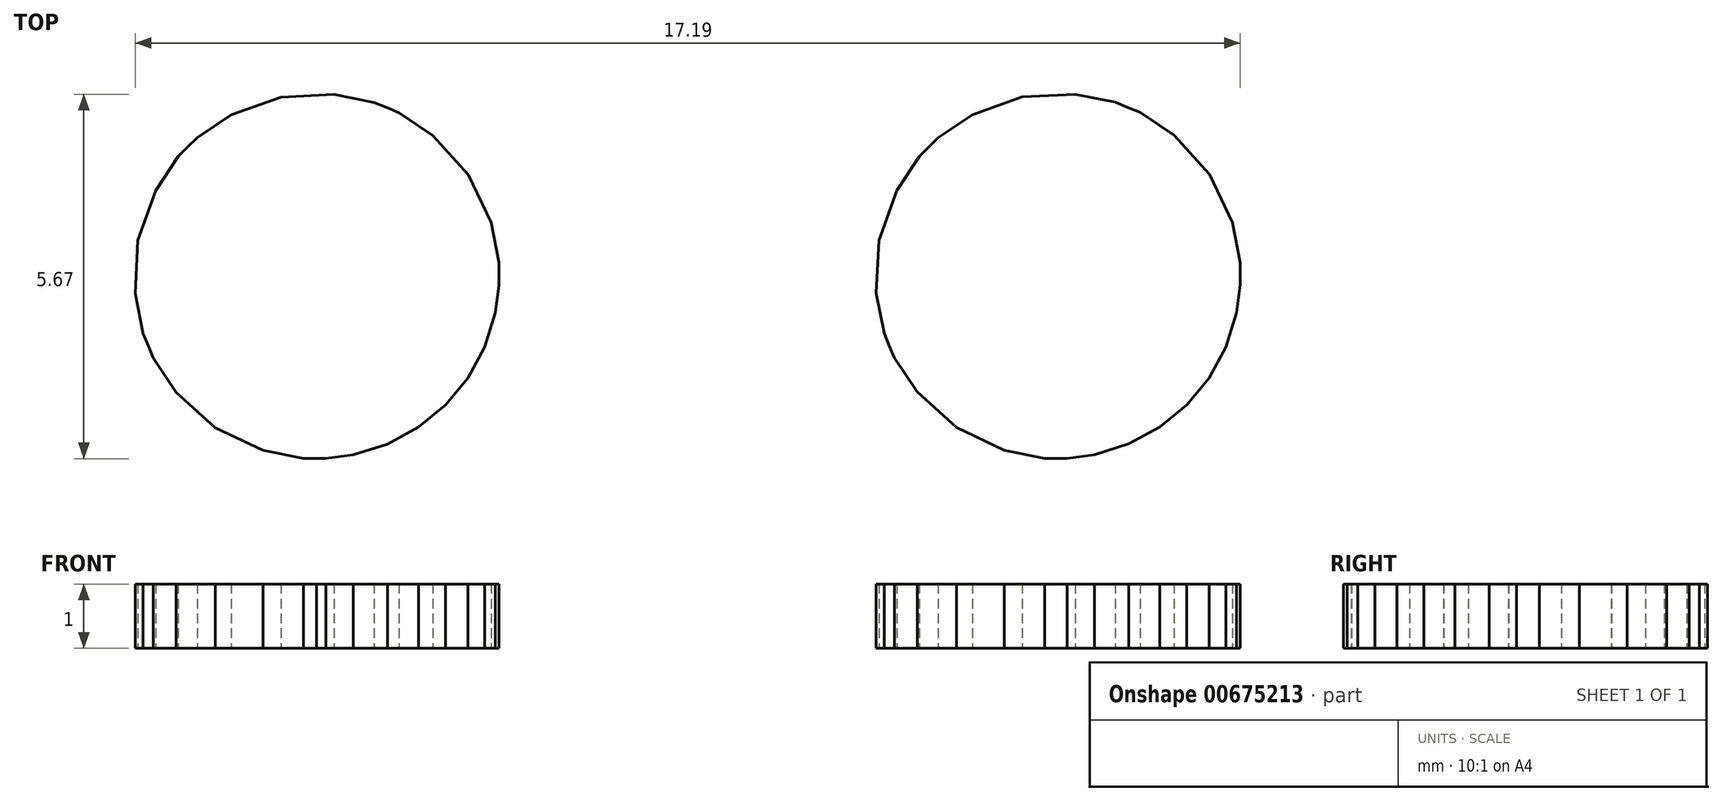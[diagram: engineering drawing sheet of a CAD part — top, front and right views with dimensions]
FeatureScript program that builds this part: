
annotation { "Feature Type Name" : "Feature", "Feature Type Description" : "" }
export const myFeature = defineFeature(function(context is Context, id is Id, definition is map)
    precondition{}
    {
        {
            var Q0;
            Q0=qCreatedBy(makeId("Top.planeOp"),FACE);
            var sketch = newSketch(context, id + "F0", { "sketchPlane" : qUnion([Q0])});
            skLineSegment(sketch, "E0", {"start": v(20.61, 4.27) * mm, "end": v(20.61, 4.15) * mm});
            skLineSegment(sketch, "E1", {"start": v(20.61, 4.15) * mm, "end": v(20.52, 3.81) * mm});
            skLineSegment(sketch, "E2", {"start": v(20.52, 3.81) * mm, "end": v(20.27, 3.44) * mm});
            skLineSegment(sketch, "E3", {"start": v(20.27, 3.44) * mm, "end": v(19.9, 3.2) * mm});
            skLineSegment(sketch, "E4", {"start": v(19.9, 3.2) * mm, "end": v(19.56, 3.1) * mm});
            skLineSegment(sketch, "E5", {"start": v(19.56, 3.1) * mm, "end": v(19.45, 3.1) * mm});
            skLineSegment(sketch, "E6", {"start": v(19.45, 3.1) * mm, "end": v(19.34, 3.1) * mm});
            skLineSegment(sketch, "E7", {"start": v(19.34, 3.1) * mm, "end": v(19, 3.2) * mm});
            skLineSegment(sketch, "E8", {"start": v(19, 3.2) * mm, "end": v(18.63, 3.44) * mm});
            skLineSegment(sketch, "E9", {"start": v(18.63, 3.44) * mm, "end": v(18.38, 3.81) * mm});
            skLineSegment(sketch, "E10", {"start": v(18.38, 3.81) * mm, "end": v(18.29, 4.15) * mm});
            skLineSegment(sketch, "E11", {"start": v(18.29, 4.15) * mm, "end": v(18.29, 4.27) * mm});
            skLineSegment(sketch, "E12", {"start": v(18.29, 4.27) * mm, "end": v(18.29, 4.38) * mm});
            skLineSegment(sketch, "E13", {"start": v(18.29, 4.38) * mm, "end": v(18.38, 4.72) * mm});
            skLineSegment(sketch, "E14", {"start": v(18.38, 4.72) * mm, "end": v(18.63, 5.09) * mm});
            skLineSegment(sketch, "E15", {"start": v(18.63, 5.09) * mm, "end": v(19, 5.34) * mm});
            skLineSegment(sketch, "E16", {"start": v(19, 5.34) * mm, "end": v(19.34, 5.43) * mm});
            skLineSegment(sketch, "E17", {"start": v(19.34, 5.43) * mm, "end": v(19.45, 5.43) * mm});
            skLineSegment(sketch, "E18", {"start": v(19.45, 5.43) * mm, "end": v(19.56, 5.43) * mm});
            skLineSegment(sketch, "E19", {"start": v(19.56, 5.43) * mm, "end": v(19.9, 5.34) * mm});
            skLineSegment(sketch, "E20", {"start": v(19.9, 5.34) * mm, "end": v(20.27, 5.09) * mm});
            skLineSegment(sketch, "E21", {"start": v(20.27, 5.09) * mm, "end": v(20.52, 4.72) * mm});
            skLineSegment(sketch, "E22", {"start": v(20.52, 4.72) * mm, "end": v(20.61, 4.38) * mm});
            skLineSegment(sketch, "E23", {"start": v(20.61, 4.38) * mm, "end": v(20.61, 4.27) * mm});
            skLineSegment(sketch, "E24", {"start": v(14.75, 8) * mm, "end": v(12.79, 8) * mm});
            skLineSegment(sketch, "E25", {"start": v(12.79, 8) * mm, "end": v(12.79, 1.6) * mm});
            skLineSegment(sketch, "E26", {"start": v(12.79, 1.6) * mm, "end": v(11.27, 1.6) * mm});
            skLineSegment(sketch, "E27", {"start": v(11.27, 1.6) * mm, "end": v(11.27, -0.27) * mm});
            skLineSegment(sketch, "E28", {"start": v(11.27, -0.27) * mm, "end": v(12.79, -0.27) * mm});
            skLineSegment(sketch, "E29", {"start": v(12.79, -0.27) * mm, "end": v(12.79, -8) * mm});
            skLineSegment(sketch, "E30", {"start": v(12.79, -8) * mm, "end": v(14.75, -8) * mm});
            skLineSegment(sketch, "E31", {"start": v(14.75, -8) * mm, "end": v(14.75, -0.27) * mm});
            skLineSegment(sketch, "E32", {"start": v(14.75, -0.27) * mm, "end": v(16.9, -0.27) * mm});
            skLineSegment(sketch, "E33", {"start": v(16.9, -0.27) * mm, "end": v(16.9, 1.56) * mm});
            skLineSegment(sketch, "E34", {"start": v(16.9, 1.56) * mm, "end": v(14.75, 1.56) * mm});
            skLineSegment(sketch, "E35", {"start": v(14.75, 1.56) * mm, "end": v(14.75, 8) * mm});
            skLineSegment(sketch, "E36", {"start": v(5.3, 1.59) * mm, "end": v(5.12, 1.59) * mm});
            skLineSegment(sketch, "E37", {"start": v(5.12, 1.59) * mm, "end": v(4.59, 1.53) * mm});
            skLineSegment(sketch, "E38", {"start": v(4.59, 1.53) * mm, "end": v(3.9, 1.38) * mm});
            skLineSegment(sketch, "E39", {"start": v(3.9, 1.38) * mm, "end": v(3.25, 1.12) * mm});
            skLineSegment(sketch, "E40", {"start": v(3.25, 1.12) * mm, "end": v(2.65, 0.78) * mm});
            skLineSegment(sketch, "E41", {"start": v(2.65, 0.78) * mm, "end": v(2.1, 0.35) * mm});
            skLineSegment(sketch, "E42", {"start": v(2.1, 0.35) * mm, "end": v(1.62, -0.15) * mm});
            skLineSegment(sketch, "E43", {"start": v(1.62, -0.15) * mm, "end": v(1.2, -0.72) * mm});
            skLineSegment(sketch, "E44", {"start": v(1.2, -0.72) * mm, "end": v(0.95, -1.2) * mm});
            skLineSegment(sketch, "E45", {"start": v(0.95, -1.2) * mm, "end": v(0.88, -1.37) * mm});
            skLineSegment(sketch, "E46", {"start": v(0.88, -1.37) * mm, "end": v(0.82, -1.53) * mm});
            skLineSegment(sketch, "E47", {"start": v(0.82, -1.53) * mm, "end": v(0.66, -2.05) * mm});
            skLineSegment(sketch, "E48", {"start": v(0.66, -2.05) * mm, "end": v(0.54, -2.74) * mm});
            skLineSegment(sketch, "E49", {"start": v(0.54, -2.74) * mm, "end": v(0.53, -3.44) * mm});
            skLineSegment(sketch, "E50", {"start": v(0.53, -3.44) * mm, "end": v(0.61, -4.13) * mm});
            skLineSegment(sketch, "E51", {"start": v(0.61, -4.13) * mm, "end": v(0.8, -4.8) * mm});
            skLineSegment(sketch, "E52", {"start": v(0.8, -4.8) * mm, "end": v(1.08, -5.44) * mm});
            skLineSegment(sketch, "E53", {"start": v(1.08, -5.44) * mm, "end": v(1.45, -6.03) * mm});
            skLineSegment(sketch, "E54", {"start": v(1.45, -6.03) * mm, "end": v(1.8, -6.45) * mm});
            skLineSegment(sketch, "E55", {"start": v(1.8, -6.45) * mm, "end": v(1.92, -6.58) * mm});
            skLineSegment(sketch, "E56", {"start": v(1.92, -6.58) * mm, "end": v(2.05, -6.7) * mm});
            skLineSegment(sketch, "E57", {"start": v(2.05, -6.7) * mm, "end": v(2.46, -7.04) * mm});
            skLineSegment(sketch, "E58", {"start": v(2.46, -7.04) * mm, "end": v(3.06, -7.42) * mm});
            skLineSegment(sketch, "E59", {"start": v(3.06, -7.42) * mm, "end": v(3.7, -7.7) * mm});
            skLineSegment(sketch, "E60", {"start": v(3.7, -7.7) * mm, "end": v(4.37, -7.89) * mm});
            skLineSegment(sketch, "E61", {"start": v(4.37, -7.89) * mm, "end": v(5.06, -7.97) * mm});
            skLineSegment(sketch, "E62", {"start": v(5.06, -7.97) * mm, "end": v(5.76, -7.96) * mm});
            skLineSegment(sketch, "E63", {"start": v(5.76, -7.96) * mm, "end": v(6.45, -7.84) * mm});
            skLineSegment(sketch, "E64", {"start": v(6.45, -7.84) * mm, "end": v(6.97, -7.68) * mm});
            skLineSegment(sketch, "E65", {"start": v(6.97, -7.68) * mm, "end": v(7.13, -7.61) * mm});
            skLineSegment(sketch, "E66", {"start": v(7.13, -7.61) * mm, "end": v(7.3, -7.55) * mm});
            skLineSegment(sketch, "E67", {"start": v(7.3, -7.55) * mm, "end": v(7.77, -7.3) * mm});
            skLineSegment(sketch, "E68", {"start": v(7.77, -7.3) * mm, "end": v(8.35, -6.88) * mm});
            skLineSegment(sketch, "E69", {"start": v(8.35, -6.88) * mm, "end": v(8.85, -6.4) * mm});
            skLineSegment(sketch, "E70", {"start": v(8.85, -6.4) * mm, "end": v(9.28, -5.85) * mm});
            skLineSegment(sketch, "E71", {"start": v(9.28, -5.85) * mm, "end": v(9.62, -5.25) * mm});
            skLineSegment(sketch, "E72", {"start": v(9.62, -5.25) * mm, "end": v(9.87, -4.6) * mm});
            skLineSegment(sketch, "E73", {"start": v(9.87, -4.6) * mm, "end": v(10.03, -3.91) * mm});
            skLineSegment(sketch, "E74", {"start": v(10.03, -3.91) * mm, "end": v(10.08, -3.37) * mm});
            skLineSegment(sketch, "E75", {"start": v(10.08, -3.37) * mm, "end": v(10.08, -3.2) * mm});
            skLineSegment(sketch, "E76", {"start": v(10.08, -3.2) * mm, "end": v(10.08, -2.95) * mm});
            skLineSegment(sketch, "E77", {"start": v(10.08, -2.95) * mm, "end": v(9.99, -2.23) * mm});
            skLineSegment(sketch, "E78", {"start": v(9.99, -2.23) * mm, "end": v(9.7, -1.33) * mm});
            skLineSegment(sketch, "E79", {"start": v(9.7, -1.33) * mm, "end": v(9.27, -0.52) * mm});
            skLineSegment(sketch, "E80", {"start": v(9.27, -0.52) * mm, "end": v(8.68, 0.19) * mm});
            skLineSegment(sketch, "E81", {"start": v(8.68, 0.19) * mm, "end": v(7.98, 0.77) * mm});
            skLineSegment(sketch, "E82", {"start": v(7.98, 0.77) * mm, "end": v(7.16, 1.21) * mm});
            skLineSegment(sketch, "E83", {"start": v(7.16, 1.21) * mm, "end": v(6.27, 1.49) * mm});
            skLineSegment(sketch, "E84", {"start": v(6.27, 1.49) * mm, "end": v(5.54, 1.59) * mm});
            skLineSegment(sketch, "E85", {"start": v(5.54, 1.59) * mm, "end": v(5.3, 1.59) * mm});
            skLineSegment(sketch, "E86", {"start": v(5.3, -6.03) * mm, "end": v(5.1, -6.03) * mm});
            skLineSegment(sketch, "E87", {"start": v(5.1, -6.03) * mm, "end": v(4.47, -5.9) * mm});
            skLineSegment(sketch, "E88", {"start": v(4.47, -5.9) * mm, "end": v(3.73, -5.55) * mm});
            skLineSegment(sketch, "E89", {"start": v(3.73, -5.55) * mm, "end": v(3.11, -5) * mm});
            skLineSegment(sketch, "E90", {"start": v(3.11, -5) * mm, "end": v(2.76, -4.47) * mm});
            skLineSegment(sketch, "E91", {"start": v(2.76, -4.47) * mm, "end": v(2.68, -4.28) * mm});
            skLineSegment(sketch, "E92", {"start": v(2.68, -4.28) * mm, "end": v(2.6, -4.09) * mm});
            skLineSegment(sketch, "E93", {"start": v(2.6, -4.09) * mm, "end": v(2.48, -3.46) * mm});
            skLineSegment(sketch, "E94", {"start": v(2.48, -3.46) * mm, "end": v(2.52, -2.64) * mm});
            skLineSegment(sketch, "E95", {"start": v(2.52, -2.64) * mm, "end": v(2.8, -1.87) * mm});
            skLineSegment(sketch, "E96", {"start": v(2.8, -1.87) * mm, "end": v(3.15, -1.34) * mm});
            skLineSegment(sketch, "E97", {"start": v(3.15, -1.34) * mm, "end": v(3.3, -1.19) * mm});
            skLineSegment(sketch, "E98", {"start": v(3.3, -1.19) * mm, "end": v(3.44, -1.04) * mm});
            skLineSegment(sketch, "E99", {"start": v(3.44, -1.04) * mm, "end": v(3.97, -0.69) * mm});
            skLineSegment(sketch, "E100", {"start": v(3.97, -0.69) * mm, "end": v(4.75, -0.41) * mm});
            skLineSegment(sketch, "E101", {"start": v(4.75, -0.41) * mm, "end": v(5.57, -0.37) * mm});
            skLineSegment(sketch, "E102", {"start": v(5.57, -0.37) * mm, "end": v(6.2, -0.5) * mm});
            skLineSegment(sketch, "E103", {"start": v(6.2, -0.5) * mm, "end": v(6.39, -0.57) * mm});
            skLineSegment(sketch, "E104", {"start": v(6.39, -0.57) * mm, "end": v(6.58, -0.65) * mm});
            skLineSegment(sketch, "E105", {"start": v(6.58, -0.65) * mm, "end": v(7.1, -1) * mm});
            skLineSegment(sketch, "E106", {"start": v(7.1, -1) * mm, "end": v(7.66, -1.62) * mm});
            skLineSegment(sketch, "E107", {"start": v(7.66, -1.62) * mm, "end": v(8.02, -2.36) * mm});
            skLineSegment(sketch, "E108", {"start": v(8.02, -2.36) * mm, "end": v(8.14, -2.99) * mm});
            skLineSegment(sketch, "E109", {"start": v(8.14, -2.99) * mm, "end": v(8.14, -3.2) * mm});
            skLineSegment(sketch, "E110", {"start": v(8.14, -3.2) * mm, "end": v(8.14, -3.34) * mm});
            skLineSegment(sketch, "E111", {"start": v(8.14, -3.34) * mm, "end": v(8.08, -3.77) * mm});
            skLineSegment(sketch, "E112", {"start": v(8.08, -3.77) * mm, "end": v(7.92, -4.3) * mm});
            skLineSegment(sketch, "E113", {"start": v(7.92, -4.3) * mm, "end": v(7.66, -4.78) * mm});
            skLineSegment(sketch, "E114", {"start": v(7.66, -4.78) * mm, "end": v(7.3, -5.2) * mm});
            skLineSegment(sketch, "E115", {"start": v(7.3, -5.2) * mm, "end": v(6.89, -5.55) * mm});
            skLineSegment(sketch, "E116", {"start": v(6.89, -5.55) * mm, "end": v(6.4, -5.81) * mm});
            skLineSegment(sketch, "E117", {"start": v(6.4, -5.81) * mm, "end": v(5.87, -5.98) * mm});
            skLineSegment(sketch, "E118", {"start": v(5.87, -5.98) * mm, "end": v(5.45, -6.03) * mm});
            skLineSegment(sketch, "E119", {"start": v(5.45, -6.03) * mm, "end": v(5.3, -6.03) * mm});
            skLineSegment(sketch, "E120", {"start": v(-1.42, 8) * mm, "end": v(-3.39, 8) * mm});
            skLineSegment(sketch, "E121", {"start": v(-3.39, 8) * mm, "end": v(-3.39, 0.65) * mm});
            skLineSegment(sketch, "E122", {"start": v(-3.39, 0.65) * mm, "end": v(-3.55, 0.77) * mm});
            skLineSegment(sketch, "E123", {"start": v(-3.55, 0.77) * mm, "end": v(-4.09, 1.08) * mm});
            skLineSegment(sketch, "E124", {"start": v(-4.09, 1.08) * mm, "end": v(-4.83, 1.38) * mm});
            skLineSegment(sketch, "E125", {"start": v(-4.83, 1.38) * mm, "end": v(-5.6, 1.55) * mm});
            skLineSegment(sketch, "E126", {"start": v(-5.6, 1.55) * mm, "end": v(-6.39, 1.58) * mm});
            skLineSegment(sketch, "E127", {"start": v(-6.39, 1.58) * mm, "end": v(-7.17, 1.5) * mm});
            skLineSegment(sketch, "E128", {"start": v(-7.17, 1.5) * mm, "end": v(-7.93, 1.28) * mm});
            skLineSegment(sketch, "E129", {"start": v(-7.93, 1.28) * mm, "end": v(-8.65, 0.93) * mm});
            skLineSegment(sketch, "E130", {"start": v(-8.65, 0.93) * mm, "end": v(-9.16, 0.59) * mm});
            skLineSegment(sketch, "E131", {"start": v(-9.16, 0.59) * mm, "end": v(-9.31, 0.46) * mm});
            skLineSegment(sketch, "E132", {"start": v(-9.31, 0.46) * mm, "end": v(-9.47, 0.33) * mm});
            skLineSegment(sketch, "E133", {"start": v(-9.47, 0.33) * mm, "end": v(-9.9, -0.12) * mm});
            skLineSegment(sketch, "E134", {"start": v(-9.9, -0.12) * mm, "end": v(-10.35, -0.78) * mm});
            skLineSegment(sketch, "E135", {"start": v(-10.35, -0.78) * mm, "end": v(-10.7, -1.49) * mm});
            skLineSegment(sketch, "E136", {"start": v(-10.7, -1.49) * mm, "end": v(-10.91, -2.24) * mm});
            skLineSegment(sketch, "E137", {"start": v(-10.91, -2.24) * mm, "end": v(-11, -3.02) * mm});
            skLineSegment(sketch, "E138", {"start": v(-11, -3.02) * mm, "end": v(-10.97, -3.81) * mm});
            skLineSegment(sketch, "E139", {"start": v(-10.97, -3.81) * mm, "end": v(-10.8, -4.6) * mm});
            skLineSegment(sketch, "E140", {"start": v(-10.8, -4.6) * mm, "end": v(-10.59, -5.17) * mm});
            skLineSegment(sketch, "E141", {"start": v(-10.59, -5.17) * mm, "end": v(-10.5, -5.35) * mm});
            skLineSegment(sketch, "E142", {"start": v(-10.5, -5.35) * mm, "end": v(-10.4, -5.53) * mm});
            skLineSegment(sketch, "E143", {"start": v(-10.4, -5.53) * mm, "end": v(-10.07, -6.05) * mm});
            skLineSegment(sketch, "E144", {"start": v(-10.07, -6.05) * mm, "end": v(-9.54, -6.65) * mm});
            skLineSegment(sketch, "E145", {"start": v(-9.54, -6.65) * mm, "end": v(-8.92, -7.14) * mm});
            skLineSegment(sketch, "E146", {"start": v(-8.92, -7.14) * mm, "end": v(-8.24, -7.53) * mm});
            skLineSegment(sketch, "E147", {"start": v(-8.24, -7.53) * mm, "end": v(-7.5, -7.8) * mm});
            skLineSegment(sketch, "E148", {"start": v(-7.5, -7.8) * mm, "end": v(-6.73, -7.95) * mm});
            skLineSegment(sketch, "E149", {"start": v(-6.73, -7.95) * mm, "end": v(-5.93, -7.97) * mm});
            skLineSegment(sketch, "E150", {"start": v(-5.93, -7.97) * mm, "end": v(-5.32, -7.9) * mm});
            skLineSegment(sketch, "E151", {"start": v(-5.32, -7.9) * mm, "end": v(-5.12, -7.85) * mm});
            skLineSegment(sketch, "E152", {"start": v(-5.12, -7.85) * mm, "end": v(-4.92, -7.8) * mm});
            skLineSegment(sketch, "E153", {"start": v(-4.92, -7.8) * mm, "end": v(-4.34, -7.6) * mm});
            skLineSegment(sketch, "E154", {"start": v(-4.34, -7.6) * mm, "end": v(-3.64, -7.22) * mm});
            skLineSegment(sketch, "E155", {"start": v(-3.64, -7.22) * mm, "end": v(-3.01, -6.73) * mm});
            skLineSegment(sketch, "E156", {"start": v(-3.01, -6.73) * mm, "end": v(-2.47, -6.16) * mm});
            skLineSegment(sketch, "E157", {"start": v(-2.47, -6.16) * mm, "end": v(-2.04, -5.5) * mm});
            skLineSegment(sketch, "E158", {"start": v(-2.04, -5.5) * mm, "end": v(-1.72, -4.78) * mm});
            skLineSegment(sketch, "E159", {"start": v(-1.72, -4.78) * mm, "end": v(-1.52, -4.01) * mm});
            skLineSegment(sketch, "E160", {"start": v(-1.52, -4.01) * mm, "end": v(-1.45, -3.4) * mm});
            skLineSegment(sketch, "E161", {"start": v(-1.45, -3.4) * mm, "end": v(-1.45, -3.2) * mm});
            skLineSegment(sketch, "E162", {"start": v(-1.45, -3.2) * mm, "end": v(-1.45, -3.19) * mm});
            skLineSegment(sketch, "E163", {"start": v(-1.45, -3.19) * mm, "end": v(-1.45, -3.18) * mm});
            skLineSegment(sketch, "E164", {"start": v(-1.45, -3.18) * mm, "end": v(-1.45, -3.17) * mm});
            skLineSegment(sketch, "E165", {"start": v(-1.45, -3.17) * mm, "end": v(-1.42, 8) * mm});
            skLineSegment(sketch, "E166", {"start": v(-6.23, -6.04) * mm, "end": v(-6.44, -6.04) * mm});
            skLineSegment(sketch, "E167", {"start": v(-6.44, -6.04) * mm, "end": v(-7.06, -5.91) * mm});
            skLineSegment(sketch, "E168", {"start": v(-7.06, -5.91) * mm, "end": v(-7.8, -5.56) * mm});
            skLineSegment(sketch, "E169", {"start": v(-7.8, -5.56) * mm, "end": v(-8.42, -5) * mm});
            skLineSegment(sketch, "E170", {"start": v(-8.42, -5) * mm, "end": v(-8.77, -4.48) * mm});
            skLineSegment(sketch, "E171", {"start": v(-8.77, -4.48) * mm, "end": v(-8.85, -4.28) * mm});
            skLineSegment(sketch, "E172", {"start": v(-8.85, -4.28) * mm, "end": v(-8.93, -4.1) * mm});
            skLineSegment(sketch, "E173", {"start": v(-8.93, -4.1) * mm, "end": v(-9.05, -3.47) * mm});
            skLineSegment(sketch, "E174", {"start": v(-9.05, -3.47) * mm, "end": v(-9.01, -2.64) * mm});
            skLineSegment(sketch, "E175", {"start": v(-9.01, -2.64) * mm, "end": v(-8.73, -1.87) * mm});
            skLineSegment(sketch, "E176", {"start": v(-8.73, -1.87) * mm, "end": v(-8.38, -1.34) * mm});
            skLineSegment(sketch, "E177", {"start": v(-8.38, -1.34) * mm, "end": v(-8.23, -1.2) * mm});
            skLineSegment(sketch, "E178", {"start": v(-8.23, -1.2) * mm, "end": v(-8.09, -1.04) * mm});
            skLineSegment(sketch, "E179", {"start": v(-8.09, -1.04) * mm, "end": v(-7.56, -0.7) * mm});
            skLineSegment(sketch, "E180", {"start": v(-7.56, -0.7) * mm, "end": v(-6.78, -0.41) * mm});
            skLineSegment(sketch, "E181", {"start": v(-6.78, -0.41) * mm, "end": v(-5.96, -0.37) * mm});
            skLineSegment(sketch, "E182", {"start": v(-5.96, -0.37) * mm, "end": v(-5.33, -0.5) * mm});
            skLineSegment(sketch, "E183", {"start": v(-5.33, -0.5) * mm, "end": v(-5.14, -0.58) * mm});
            skLineSegment(sketch, "E184", {"start": v(-5.14, -0.58) * mm, "end": v(-4.95, -0.66) * mm});
            skLineSegment(sketch, "E185", {"start": v(-4.95, -0.66) * mm, "end": v(-4.42, -1) * mm});
            skLineSegment(sketch, "E186", {"start": v(-4.42, -1) * mm, "end": v(-3.87, -1.62) * mm});
            skLineSegment(sketch, "E187", {"start": v(-3.87, -1.62) * mm, "end": v(-3.51, -2.37) * mm});
            skLineSegment(sketch, "E188", {"start": v(-3.51, -2.37) * mm, "end": v(-3.39, -2.99) * mm});
            skLineSegment(sketch, "E189", {"start": v(-3.39, -2.99) * mm, "end": v(-3.39, -3.2) * mm});
            skLineSegment(sketch, "E190", {"start": v(-3.39, -3.2) * mm, "end": v(-3.39, -3.34) * mm});
            skLineSegment(sketch, "E191", {"start": v(-3.39, -3.34) * mm, "end": v(-3.45, -3.77) * mm});
            skLineSegment(sketch, "E192", {"start": v(-3.45, -3.77) * mm, "end": v(-3.61, -4.3) * mm});
            skLineSegment(sketch, "E193", {"start": v(-3.61, -4.3) * mm, "end": v(-3.88, -4.78) * mm});
            skLineSegment(sketch, "E194", {"start": v(-3.88, -4.78) * mm, "end": v(-4.22, -5.2) * mm});
            skLineSegment(sketch, "E195", {"start": v(-4.22, -5.2) * mm, "end": v(-4.64, -5.55) * mm});
            skLineSegment(sketch, "E196", {"start": v(-4.64, -5.55) * mm, "end": v(-5.12, -5.81) * mm});
            skLineSegment(sketch, "E197", {"start": v(-5.12, -5.81) * mm, "end": v(-5.66, -5.98) * mm});
            skLineSegment(sketch, "E198", {"start": v(-5.66, -5.98) * mm, "end": v(-6.09, -6.03) * mm});
            skLineSegment(sketch, "E199", {"start": v(-6.09, -6.03) * mm, "end": v(-6.23, -6.03) * mm});
            skLineSegment(sketch, "E200", {"start": v(-6.23, -6.03) * mm, "end": v(-6.23, -6.04) * mm});
            skLineSegment(sketch, "E201", {"start": v(-12.35, -6.82) * mm, "end": v(-12.35, -6.93) * mm});
            skLineSegment(sketch, "E202", {"start": v(-12.35, -6.93) * mm, "end": v(-12.44, -7.27) * mm});
            skLineSegment(sketch, "E203", {"start": v(-12.44, -7.27) * mm, "end": v(-12.7, -7.64) * mm});
            skLineSegment(sketch, "E204", {"start": v(-12.7, -7.64) * mm, "end": v(-13.06, -7.89) * mm});
            skLineSegment(sketch, "E205", {"start": v(-13.06, -7.89) * mm, "end": v(-13.4, -7.98) * mm});
            skLineSegment(sketch, "E206", {"start": v(-13.4, -7.98) * mm, "end": v(-13.51, -7.98) * mm});
            skLineSegment(sketch, "E207", {"start": v(-13.51, -7.98) * mm, "end": v(-13.63, -7.98) * mm});
            skLineSegment(sketch, "E208", {"start": v(-13.63, -7.98) * mm, "end": v(-13.96, -7.89) * mm});
            skLineSegment(sketch, "E209", {"start": v(-13.96, -7.89) * mm, "end": v(-14.33, -7.64) * mm});
            skLineSegment(sketch, "E210", {"start": v(-14.33, -7.64) * mm, "end": v(-14.58, -7.27) * mm});
            skLineSegment(sketch, "E211", {"start": v(-14.58, -7.27) * mm, "end": v(-14.67, -6.93) * mm});
            skLineSegment(sketch, "E212", {"start": v(-14.67, -6.93) * mm, "end": v(-14.67, -6.82) * mm});
            skLineSegment(sketch, "E213", {"start": v(-14.67, -6.82) * mm, "end": v(-14.67, -6.7) * mm});
            skLineSegment(sketch, "E214", {"start": v(-14.67, -6.7) * mm, "end": v(-14.58, -6.36) * mm});
            skLineSegment(sketch, "E215", {"start": v(-14.58, -6.36) * mm, "end": v(-14.33, -6) * mm});
            skLineSegment(sketch, "E216", {"start": v(-14.33, -6) * mm, "end": v(-13.96, -5.74) * mm});
            skLineSegment(sketch, "E217", {"start": v(-13.96, -5.74) * mm, "end": v(-13.63, -5.65) * mm});
            skLineSegment(sketch, "E218", {"start": v(-13.63, -5.65) * mm, "end": v(-13.51, -5.65) * mm});
            skLineSegment(sketch, "E219", {"start": v(-13.51, -5.65) * mm, "end": v(-13.4, -5.65) * mm});
            skLineSegment(sketch, "E220", {"start": v(-13.4, -5.65) * mm, "end": v(-13.06, -5.74) * mm});
            skLineSegment(sketch, "E221", {"start": v(-13.06, -5.74) * mm, "end": v(-12.7, -6) * mm});
            skLineSegment(sketch, "E222", {"start": v(-12.7, -6) * mm, "end": v(-12.44, -6.36) * mm});
            skLineSegment(sketch, "E223", {"start": v(-12.44, -6.36) * mm, "end": v(-12.35, -6.7) * mm});
            skLineSegment(sketch, "E224", {"start": v(-12.35, -6.7) * mm, "end": v(-12.35, -6.82) * mm});
            skLineSegment(sketch, "E225", {"start": v(-14.53, -0.5) * mm, "end": v(-14.6, -0.48) * mm});
            skLineSegment(sketch, "E226", {"start": v(-14.6, -0.48) * mm, "end": v(-14.97, -0.41) * mm});
            skLineSegment(sketch, "E227", {"start": v(-14.97, -0.41) * mm, "end": v(-15.34, -0.4) * mm});
            skLineSegment(sketch, "E228", {"start": v(-15.34, -0.4) * mm, "end": v(-15.41, -0.4) * mm});
            skLineSegment(sketch, "E229", {"start": v(-15.41, -0.4) * mm, "end": v(-15.58, -0.4) * mm});
            skLineSegment(sketch, "E230", {"start": v(-15.58, -0.4) * mm, "end": v(-16.1, -0.44) * mm});
            skLineSegment(sketch, "E231", {"start": v(-16.1, -0.44) * mm, "end": v(-16.73, -0.6) * mm});
            skLineSegment(sketch, "E232", {"start": v(-16.73, -0.6) * mm, "end": v(-17.28, -0.86) * mm});
            skLineSegment(sketch, "E233", {"start": v(-17.28, -0.86) * mm, "end": v(-17.76, -1.24) * mm});
            skLineSegment(sketch, "E234", {"start": v(-17.76, -1.24) * mm, "end": v(-18.14, -1.72) * mm});
            skLineSegment(sketch, "E235", {"start": v(-18.14, -1.72) * mm, "end": v(-18.43, -2.32) * mm});
            skLineSegment(sketch, "E236", {"start": v(-18.43, -2.32) * mm, "end": v(-18.6, -3.03) * mm});
            skLineSegment(sketch, "E237", {"start": v(-18.6, -3.03) * mm, "end": v(-18.67, -3.66) * mm});
            skLineSegment(sketch, "E238", {"start": v(-18.67, -3.66) * mm, "end": v(-18.67, -3.87) * mm});
            skLineSegment(sketch, "E239", {"start": v(-18.67, -3.87) * mm, "end": v(-18.67, -8) * mm});
            skLineSegment(sketch, "E240", {"start": v(-18.67, -8) * mm, "end": v(-20.61, -8) * mm});
            skLineSegment(sketch, "E241", {"start": v(-20.61, -8) * mm, "end": v(-20.61, 1.58) * mm});
            skLineSegment(sketch, "E242", {"start": v(-20.61, 1.58) * mm, "end": v(-18.67, 1.58) * mm});
            skLineSegment(sketch, "E243", {"start": v(-18.67, 1.58) * mm, "end": v(-18.67, 0.33) * mm});
            skLineSegment(sketch, "E244", {"start": v(-18.67, 0.33) * mm, "end": v(-18.63, 0.42) * mm});
            skLineSegment(sketch, "E245", {"start": v(-18.63, 0.42) * mm, "end": v(-18.46, 0.65) * mm});
            skLineSegment(sketch, "E246", {"start": v(-18.46, 0.65) * mm, "end": v(-18.16, 0.92) * mm});
            skLineSegment(sketch, "E247", {"start": v(-18.16, 0.92) * mm, "end": v(-17.78, 1.16) * mm});
            skLineSegment(sketch, "E248", {"start": v(-17.78, 1.16) * mm, "end": v(-17.35, 1.35) * mm});
            skLineSegment(sketch, "E249", {"start": v(-17.35, 1.35) * mm, "end": v(-16.89, 1.5) * mm});
            skLineSegment(sketch, "E250", {"start": v(-16.89, 1.5) * mm, "end": v(-16.4, 1.61) * mm});
            skLineSegment(sketch, "E251", {"start": v(-16.4, 1.61) * mm, "end": v(-15.9, 1.68) * mm});
            skLineSegment(sketch, "E252", {"start": v(-15.9, 1.68) * mm, "end": v(-15.53, 1.7) * mm});
            skLineSegment(sketch, "E253", {"start": v(-15.53, 1.7) * mm, "end": v(-15.41, 1.7) * mm});
            skLineSegment(sketch, "E254", {"start": v(-15.41, 1.7) * mm, "end": v(-15.3, 1.7) * mm});
            skLineSegment(sketch, "E255", {"start": v(-15.3, 1.7) * mm, "end": v(-14.93, 1.67) * mm});
            skLineSegment(sketch, "E256", {"start": v(-14.93, 1.67) * mm, "end": v(-14.59, 1.59) * mm});
            skLineSegment(sketch, "E257", {"start": v(-14.59, 1.59) * mm, "end": v(-14.53, 1.56) * mm});
            skLineSegment(sketch, "E258", {"start": v(-14.53, 1.56) * mm, "end": v(-14.53, -0.5) * mm});
            skCircle(sketch, "E259", {"center": v(0, 0) * mm, "radius": 25.5 * mm});
            skSolve(sketch);
        }
        {
            var Q0;
            Q0=makeQuery(id+"F0.imprint","IMPRINT",FACE,{"disambiguationData":[TD([[makeQuery(id+"F0.imprint","IMPRINT",EDGE,{"derivedFrom":sQuery(id+"F0.wireOp",EDGE,"E166")}),-1.0]])]});
            var Q1;
            Q1=makeQuery(id+"F0.imprint","IMPRINT",FACE,{"disambiguationData":[TD([[makeQuery(id+"F0.imprint","IMPRINT",EDGE,{"derivedFrom":sQuery(id+"F0.wireOp",EDGE,"E86")}),-1.0]])]});
            extrude(context, id + "F1", {"entities" : qUnion([Q0, Q1]), "depth" : 1 * mm, "offsetDistance" : 25 * mm});
        }
    });
